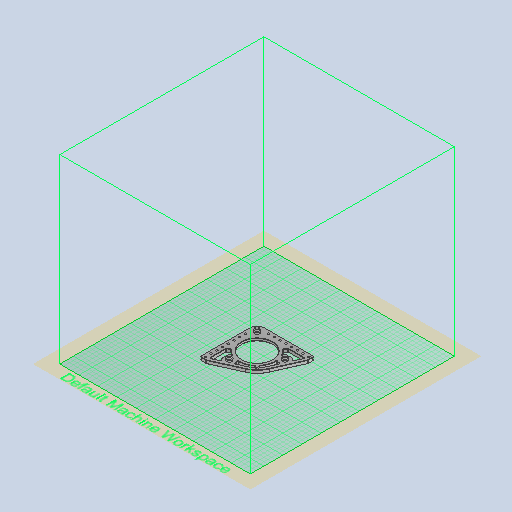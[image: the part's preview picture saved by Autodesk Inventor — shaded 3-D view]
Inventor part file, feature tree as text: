
AUTODESK INVENTOR PART (.ipt)
format: ipt  version: 2022 (Build 260153000, 153)  size: 912,896 bytes
history: native  units: in
note: dims shown in document units (in); Inventor stores cm internally (conversion verified against a paired STEP export)
features: chamfer x5, extrude x4, sketch x3, other x3, fillet x2, plane x1, pattern_circular x1, reference x1, projected_geometry x1
ambient origin geometry x8: Origin, YZ Plane, XZ Plane, XY Plane, X Axis, Y Axis, Z Axis, Center Point
bodies: Solid1 (feature_tree)
feature tree (21):
  plane  "Work Plane1"
  extrude  "Extrusion1"  Depth=0.55in
  fillet  "Fillet1"  [1 undecoded]
  chamfer  "Chamfer1"  Distance=0.3937in
  chamfer  "Chamfer2"  Distance=4.7in
  chamfer  "Chamfer3"  Distance=0.2756in
  extrude  "Extrusion4"  Depth=0.125in
  extrude  "Extrusion5"  Depth=0.125in TaperAngle=45.0deg
  chamfer  "Chamfer5"  Distance=0.125in Angle=45.0deg
  pattern_circular  "Circular Pattern1"  Angle=45.0deg  [1 undecoded]
  extrude  "Extrusion6"  Depth=0.125in
  fillet  "Fillet3"  Radius=0.9449in
  chamfer  "Chamfer6"  Distance=1.1811in
  reference  "Reference1"
  sketch  "Sketch4"  dims[d0=0.1713in d11=0.55in d12=45.0deg]
  sketch  "Sketch5"  dims[d13=0.1679in]
  sketch  "Sketch6"  dims[d14=3.0in d15=1.5748in d17=0.5in d18=0.3937in d20=1.0in d23=4.7in d24=0.2756in d25=0.0in d26=0.125in d27=0.1in d28=0.125in d29=45.0deg d30=0.0236in d31=0.125in d32=45.0deg d33=0.0236in d34=0.125in d35=45.0deg d47=0.0059in d48=0.9449in d49=1.1811in d50=0.311in d51=0.315in d52=0.0in d53=0.4764in d54=0.1181in d55=0.0in d56=0.0236in d57=0.125in d58=45.0deg d59=1.1811in d60=360.0deg d62=0.25in d63=0.25in d64=0.25in d65=0.55in d66=0.55in d67=0.25in d68=0.25in d69=45.0deg d70=0.25in d71=0.0in d72=0.0in d73=0.0394in d74=0.0236in d75=0.125in d76=45.0deg d89=1.9685in d91=0.5in d92=0.3937in d94=1.0in d96=0.1679in d99=0.125in]
  projected_geometry  "Projected Loop10"
  other  "<userpath>\Documents\CAD\guardSwerve1\Assembly1.iam"
  other  "Assembly1.iam"
  other  "Undercarriage:1"
note: 2 required parameter values undecoded (feature->parameter linkage not recoverable at this tier; creation-order binding heuristic only, values carry confidence <= 0.55)
